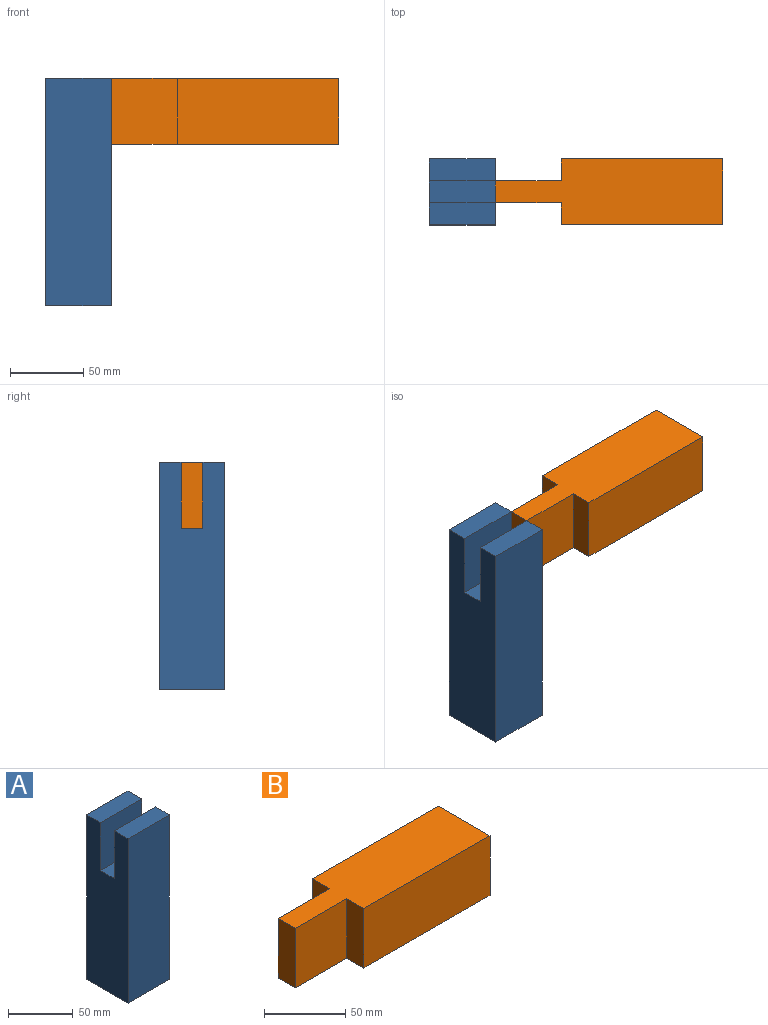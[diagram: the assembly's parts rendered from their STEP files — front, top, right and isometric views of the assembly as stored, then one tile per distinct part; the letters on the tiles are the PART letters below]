
ASSEMBLY  parts=2 mates=1
PART A: 10 faces, bbox 45x45x155 mm
  f0: plane 45x15mm, normal (0,0,1), area 675mm2, adj f1,f4,f5,f9
  f1: plane 155x45mm, normal (-1,0,0), area 6300mm2, adj f0,f2,f3,f5,f6,f7,f8,f9
  f2: plane 45x15mm, normal (0,0,1), area 675mm2, adj f1,f4,f6,f7
  f3: plane 45x45mm, normal (0,0,-1), area 2025mm2, adj f1,f4,f5,f6
  f4: plane 155x45mm, normal (1,0,0), area 6300mm2, adj f0,f2,f3,f5,f6,f7,f8,f9
  f5: plane 155x45mm, normal (0,-1,0), area 6975mm2, adj f0,f1,f3,f4
  f6: plane 155x45mm, normal (0,1,0), area 6975mm2, adj f1,f2,f3,f4
  f7: plane 45x45mm, normal (0,-1,0), area 2025mm2, adj f1,f2,f4,f8
  f8: plane 45x15mm, normal (0,0,1), area 675mm2, adj f1,f4,f7,f9
  f9: plane 45x45mm, normal (0,1,0), area 2025mm2, adj f0,f1,f4,f8
PART B: 10 faces, bbox 155x45x45 mm
  f0: plane 155x45mm, normal (0,0,1), area 5625mm2, adj f1,f2,f3,f5,f6,f7,f8,f9
  f1: plane 45x15mm, normal (-1,0,0), area 675mm2, adj f0,f4,f6,f8
  f2: plane 110x45mm, normal (0,-1,0), area 4950mm2, adj f0,f4,f5,f9
  f3: plane 110x45mm, normal (0,1,0), area 4950mm2, adj f0,f4,f5,f7
  f4: plane 155x45mm, normal (0,0,-1), area 5625mm2, adj f1,f2,f3,f5,f6,f7,f8,f9
  f5: plane 45x45mm, normal (1,0,0), area 2025mm2, adj f0,f2,f3,f4
  f6: plane 45x45mm, normal (0,1,0), area 2025mm2, adj f0,f1,f4,f7
  f7: plane 45x15mm, normal (-1,0,0), area 675mm2, adj f0,f3,f4,f6
  f8: plane 45x45mm, normal (0,-1,0), area 2025mm2, adj f0,f1,f4,f9
  f9: plane 45x15mm, normal (-1,0,0), area 675mm2, adj f0,f2,f4,f8
PLACE A t=(-22.15,59.52,-36.4)mm
PLACE B t=(77.85,59.52,18.6)mm
MATE slider A.f4 <-> B.f1  axis (1,0,0) through (0.35,59.52,-3.9)mm
